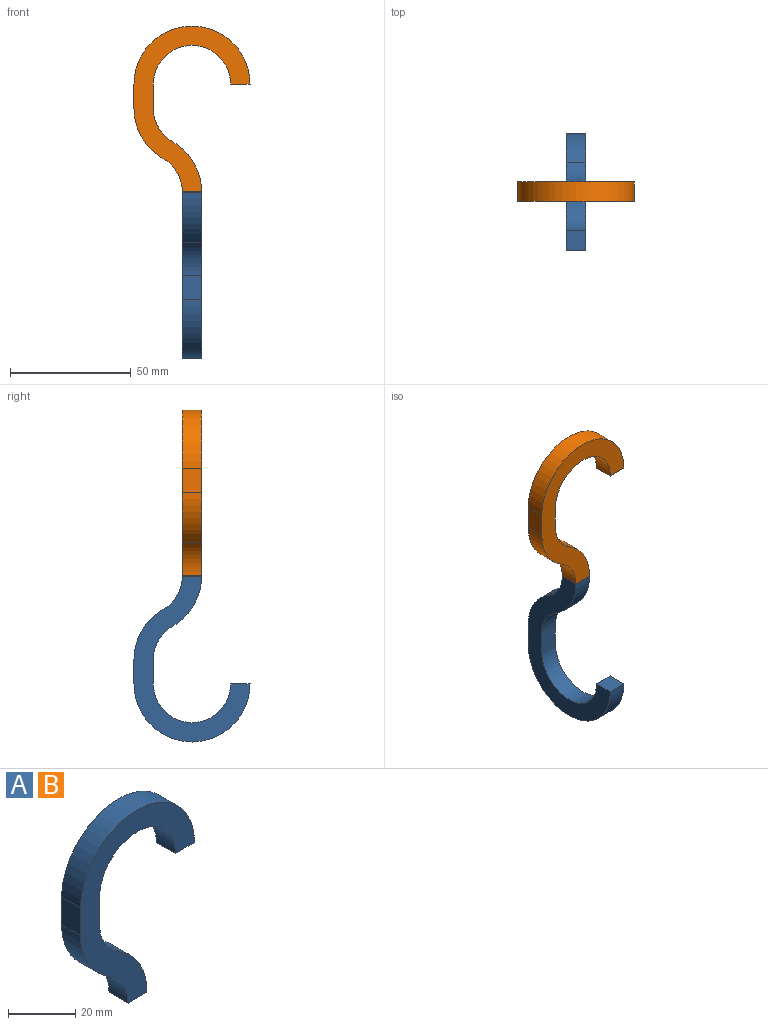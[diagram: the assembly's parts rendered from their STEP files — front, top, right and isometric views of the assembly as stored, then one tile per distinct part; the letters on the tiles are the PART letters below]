
ASSEMBLY  parts=2 mates=1
PART A: 12 faces, bbox 48x8x68.6 mm
  f0: plane 8x8mm, normal (0,0,-1), area 64mm2, adj f2,f3,f4,f5
  f1: plane 8x8mm, normal (0,0,-1), area 64mm2, adj f2,f4,f10,f11
  f2: plane 68.64x48mm, normal (0,-1,0), area 917.8mm2, adj f0,f1,f3,f5,f6,f7,f8,f9
  f3: cylinder r=24mm len=48mm, axis (0,-1,0), area 603.2mm2, adj f0,f2,f4,f6
  f4: plane 68.64x48mm, normal (0,1,0), area 917.8mm2, adj f0,f1,f3,f5,f6,f7,f8,f9
  f5: cylinder r=16mm len=32mm, axis (0,-1,0), area 402.1mm2, adj f0,f2,f4,f7
  f6: plane 10x8mm, normal (-1,0,0), area 80mm2, adj f2,f3,f4,f8
  f7: plane 10x8mm, normal (1,0,0), area 80mm2, adj f2,f4,f5,f9
  f8: cylinder r=24mm len=20.78mm, axis (0,-1,0), area 201.1mm2, adj f2,f4,f6,f10
  f9: cylinder r=16mm len=13.86mm, axis (0,-1,0), area 134mm2, adj f2,f4,f7,f11
  f10: cylinder r=16mm len=13.86mm, axis (0,1,0), area 134mm2, adj f1,f2,f4,f8
  f11: cylinder r=24mm len=20.78mm, axis (0,1,0), area 201.1mm2, adj f1,f2,f4,f9
PART B: same geometry as A
PLACE A rot(axis=(0.71,-0.71,0),180deg) t=(0,0,-89.28)mm
PLACE B at identity fixed
MATE fastened A.f1 <-> B.f1  axis (0,0,1) through (0,0,-44.64)mm
